# Revit family: Faucet-Lavatory-KOHLER-STRAYT-K-37327T.rfa_
name_source: partatom
category: Plumbing Fixtures
units: mm (PartAtom-declared; Revit-internal decimal feet)

## family parameters
Cut with Voids When Loaded = No
Host = Face
OmniClass Number = 23.31.11.00
OmniClass Title = Faucets
Part Type = Normal
Room Calculation Point = No
Round Connector Dimension = Use Diameter
Shared = No

## types (6) — shared parameters
ADA Compliant = No
Assembly Code = D2010
CW Connection = Yes
Cold Water Inlet = Cold Water Inlet
Date Modified = 09/15/2023
Default Elevation = 36"
Description = Single Basin Faucet
Drain Included = Yes
Finish = Kohler-Metal-CP-Polished_Chrome
HW Connection = Yes
Handle Clearance = 3 1/4"
Height = 7"
Hot Water Inlet = Hot Water Inlet
Length = 4 1/16"
Manufacturer = Kohler Co.
Master Format 2014 = 22 41 39
Master Format 2014 Name = Residential Faucets, Supplies, and Trim
Material = Premium Metal Construction
Product Documentation Link = https://files.kohler.com.cn
Product Name = Strayt
Spout Reach = 4 1/16"
URL = http://www.kohler.com.cn
Vent Connection = No
Waste Connection = No
Waste Water Outlet = Waste Water Outlet
WaterSense Certified = No
Width = 1 13/16"

## per-type parameters (varying)
| type | 4-Cable | B4-Cable | Flow Rate | Handle Finish | Handle With Red Design | Handle With White  Design | Handle Without Design | Model | Pressure | Product Page URL | Type |
| 4, CP-Polished Chrome | Yes | No | 0 GPM | Kohler-Metal-CP-Polished_Chrome | No | No | Yes | K-37327T-4-CP | 0.00 psi |  | 1 |
| 4DPR, CP-Polished Chrome | Yes | No | 0 GPM | Plastic-Pantone-7620C | Yes | No | No | K-37327T-4DPR-CP | 0.00 psi | https://www.kohler.com.cn | 2 |
| 4DPW, CP-Polished Chrome | Yes | No | 0 GPM | Kohler-Plastic-0-White | No | Yes | No | K-37327T-4DPW-CP | 0.00 psi | https://www.kohler.com.cn | 3 |
| B4, CP-Polished Chrome | No | Yes | 2 GPM | Kohler-Metal-CP-Polished_Chrome | No | No | Yes | K-37327T-B4-CP | 0.00 psi | https://www.kohler.com.cn | 4 |
| B4DPR, CP-Polished Chrome | No | Yes | 2 GPM | Plastic-Pantone-7620C | Yes | No | No | K-37327T-B4DPR-CP | 45.00 psi |  | 5 |
| B4DPW, CP-Polished Chrome | No | Yes | 2 GPM | Kohler-Plastic-0-White | No | Yes | No | K-37327T-B4DPW-CP | 45.00 psi |  | 6 |

## geometry (parser evidence)
native form markers: Sweep x4
no freeform markers — native parametric forms only
